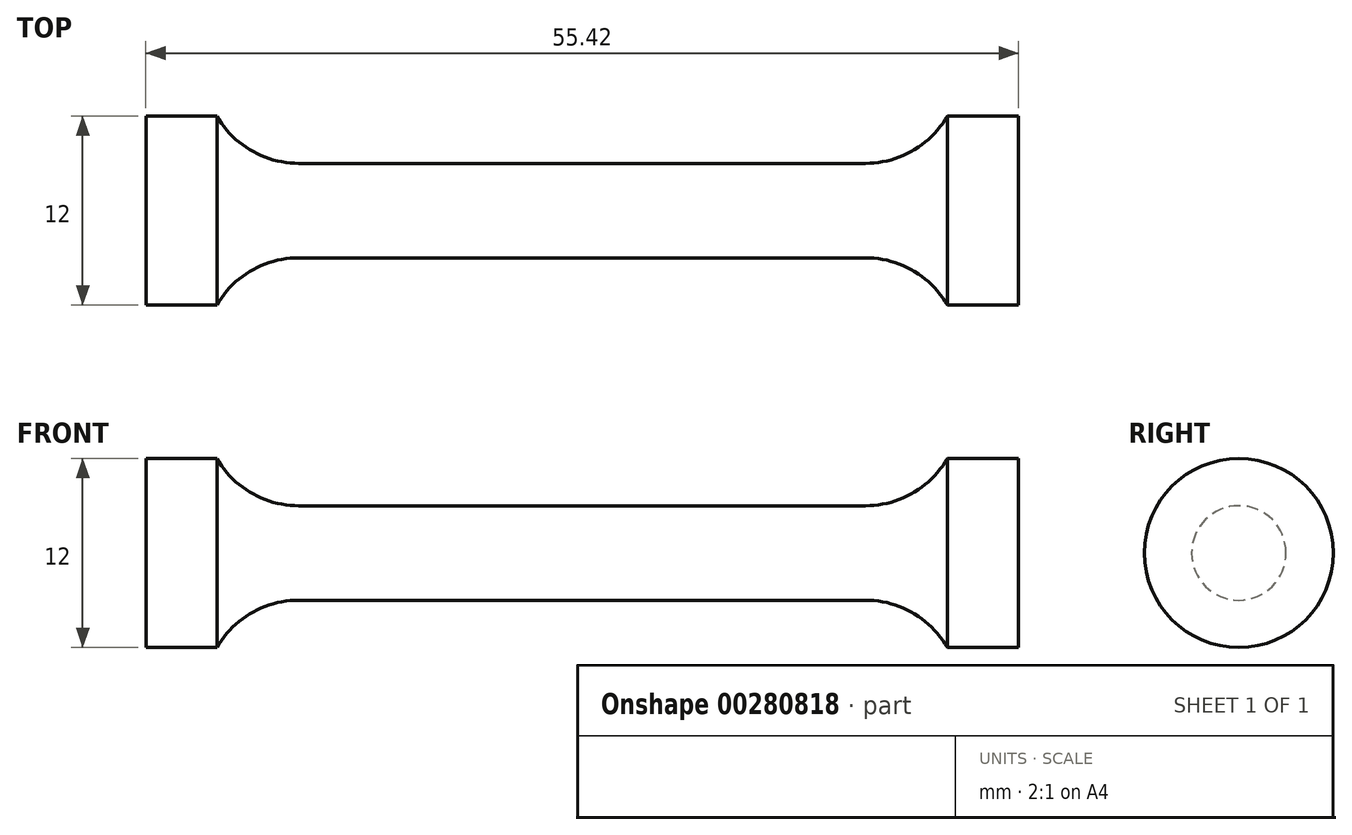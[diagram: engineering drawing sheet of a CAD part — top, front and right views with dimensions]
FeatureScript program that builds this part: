
annotation { "Feature Type Name" : "Feature", "Feature Type Description" : "" }
export const myFeature = defineFeature(function(context is Context, id is Id, definition is map)
    precondition{}
    {
        {
            var Q0;
            Q0=qCreatedBy(makeId("Front.planeOp"),FACE);
            var sketch = newSketch(context, id + "F0", { "sketchPlane" : qUnion([Q0])});
            skLineSegment(sketch, "E0", {"start": v(0, 3) * mm, "end": v(18, 3) * mm});
            skArc(sketch, "E1", {"start": v(18, 3) * mm, "mid": v(21, 3.8) * mm, "end": v(23.2, 6) * mm});
            skLineSegment(sketch, "E2", {"start": v(23.2, 6) * mm, "end": v(27.7, 6) * mm});
            skLineSegment(sketch, "E3", {"start": v(27.7, 6) * mm, "end": v(27.7, 0) * mm});
            skLineSegment(sketch, "E4.MirrorCS", {"start": v(0, 3) * mm, "end": v(-18, 3) * mm});
            skLineSegment(sketch, "E5.MirrorCS", {"start": v(-27.7, 6) * mm, "end": v(-27.7, 0) * mm});
            skLineSegment(sketch, "E6.MirrorCS", {"start": v(-23.2, 6) * mm, "end": v(-27.7, 6) * mm});
            skArc(sketch, "E7.MirrorCS", {"start": v(-18, 3) * mm, "mid": v(-21, 3.8) * mm, "end": v(-23.2, 6) * mm});
            skLineSegment(sketch, "E8", {"start": v(-27.7, 0) * mm, "end": v(27.7, 0) * mm});
            skSolve(sketch);
        }
        {
            var Q0;
            Q0=makeQuery(id+"F0.imprint","IMPRINT",FACE,{"disambiguationData":[TD([[makeQuery(id+"F0.imprint","IMPRINT",EDGE,{"derivedFrom":sQuery(id+"F0.wireOp",EDGE,"E0")}),-1.0]])]});
            var Q1;
            Q1=sQuery(id+"F0.wireOp",EDGE,"E8");
            revolve(context, id + "F1", {"entities" : qUnion([Q0]), "axis" : qUnion([Q1]), "revolveType" : RevolveType.FULL});
        }
    });
